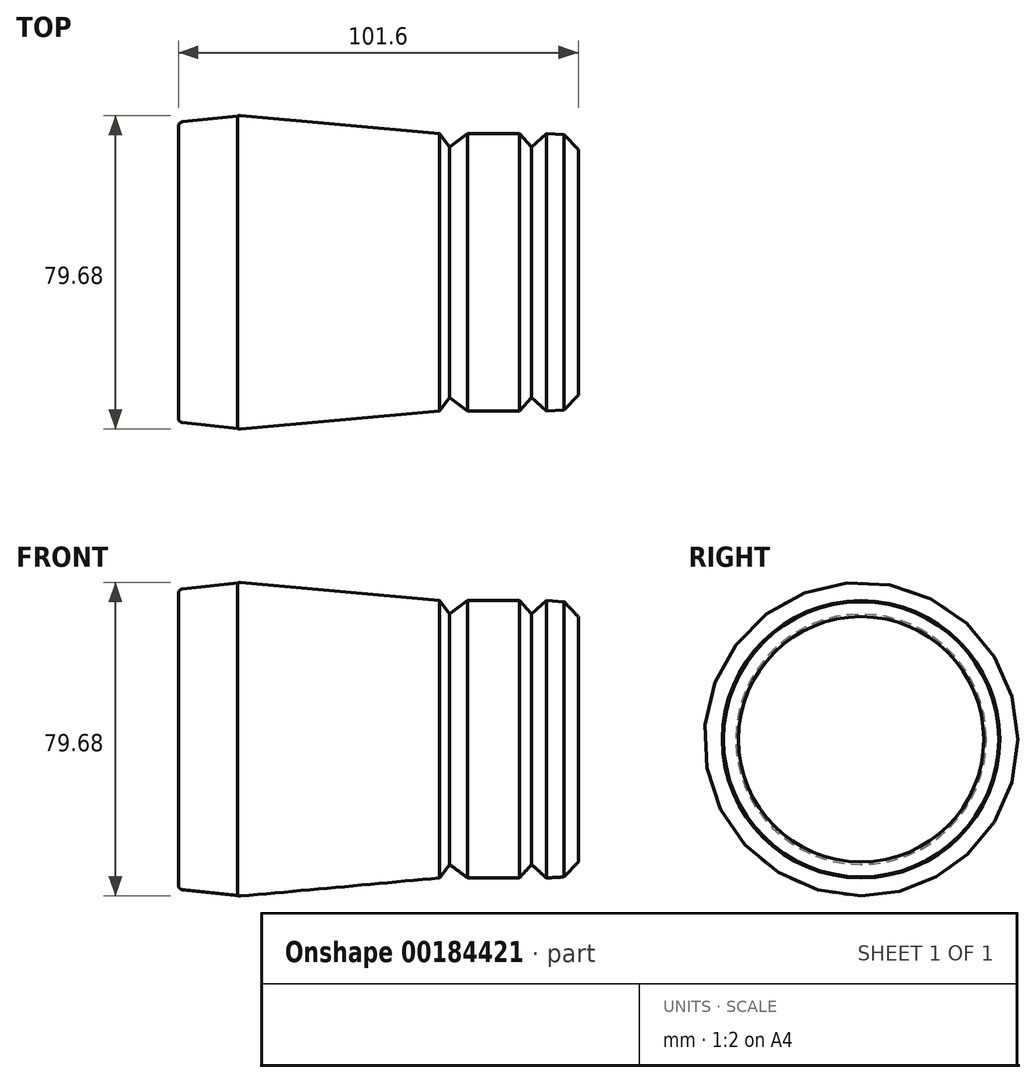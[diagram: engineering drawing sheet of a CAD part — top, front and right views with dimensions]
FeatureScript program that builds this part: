
annotation { "Feature Type Name" : "Feature", "Feature Type Description" : "" }
export const myFeature = defineFeature(function(context is Context, id is Id, definition is map)
    precondition{}
    {
        {
            var Q0;
            Q0=qCreatedBy(makeId("Front.planeOp"),FACE);
            var sketch = newSketch(context, id + "F0", { "sketchPlane" : qUnion([Q0])});
            skLineSegment(sketch, "E0", {"start": v(-60.66, 0) * mm, "end": v(-60.66, 41.28) * mm});
            skLineSegment(sketch, "E1", {"start": v(40.94, 34.75) * mm, "end": v(40.94, 0) * mm});
            skLineSegment(sketch, "E2", {"start": v(40.94, 0) * mm, "end": v(-60.66, 0) * mm});
            skLineSegment(sketch, "E3", {"start": v(-60.66, 41.28) * mm, "end": v(5.7, 35.23) * mm});
            skLineSegment(sketch, "E4", {"start": v(5.7, 35.23) * mm, "end": v(8.27, 31.8) * mm});
            skLineSegment(sketch, "E5", {"start": v(8.27, 31.8) * mm, "end": v(12.84, 35.23) * mm});
            skLineSegment(sketch, "E6", {"start": v(12.84, 35.23) * mm, "end": v(25.96, 35.23) * mm});
            skLineSegment(sketch, "E7", {"start": v(25.96, 35.23) * mm, "end": v(29.1, 31.8) * mm});
            skLineSegment(sketch, "E8", {"start": v(29.1, 31.8) * mm, "end": v(32.83, 35.23) * mm});
            skLineSegment(sketch, "E9", {"start": v(32.83, 35.23) * mm, "end": v(40.94, 34.75) * mm});
            skSolve(sketch);
        }
        {
            var Q0;
            Q0=makeQuery(id+"F0.imprint","IMPRINT",FACE,{"disambiguationData":[TD([[makeQuery(id+"F0.imprint","IMPRINT",EDGE,{"derivedFrom":sQuery(id+"F0.wireOp",EDGE,"E0")}),-1.0]])]});
            var Q1;
            Q1=sQuery(id+"F0.wireOp",EDGE,"E2");
            revolve(context, id + "F1", {"entities" : qUnion([Q0]), "axis" : qUnion([Q1]), "revolveType" : RevolveType.FULL});
        }
        {
            var Q0;
            Q0=makeQuery(id+"F1.opRevolve","SWEPT_FACE",FACE,{"disambiguationData":[OSD([sQuery(id+"F0.wireOp",EDGE,"E0")])]});
            var sketch = newSketch(context, id + "F2", { "sketchPlane" : qUnion([Q0])});
            skCircle(sketch, "E10.0", {"center": v(0, 0) * mm, "radius": 38.1 * mm});
            skSolve(sketch);
        }
        {
            var Q0;
            Q0=makeQuery(id+"F2.imprint","IMPRINT",FACE,{"disambiguationData":[TD([[makeQuery(id+"F2.imprint","IMPRINT",EDGE,{"derivedFrom":sQuery(id+"F2.wireOp",EDGE,"E10.0")}),-1.0]])]});
            extrude(context, id + "F3", {"entities" : qUnion([Q0]), "operationType" : NewBodyOperationType.REMOVE, "oppositeDirection" : true, "depth" : 82.55 * mm, "hasDraft" : true, "draftAngle" : 6 * degree, "draftPullDirection" : true});
        }
        {
            var Q0;
            Q0=makeQuery(id+"F1.opRevolve","SWEPT_EDGE",EDGE,{"disambiguationData":[OSD([sQuery(id+"F0.wireOp",EDGE,"E1"),sQuery(id+"F0.wireOp",EDGE,"E9")])]});
            chamfer(context, id + "F4", {"entities" : qUnion([Q0]), "width" : 3.8 * mm, "tangentPropagation" : true});
        }
        {
            var Q0;
            Q0=makeQuery(id+"F1.opRevolve","SWEPT_EDGE",EDGE,{"disambiguationData":[OSD([sQuery(id+"F0.wireOp",EDGE,"E0"),sQuery(id+"F0.wireOp",EDGE,"E3")])]});
            fillet(context, id + "F5", {"entities" : qUnion([Q0]), "radius" : 1.27 * mm, "tangentPropagation" : true, "allowEdgeOverflow" : false});
        }
        {
            var Q0;
            Q0=makeQuery(id+"F1.opRevolve","SWEPT_FACE",FACE,{"disambiguationData":[OSD([sQuery(id+"F0.wireOp",EDGE,"E0")])]});
            fillet(context, id + "F6", {"entities" : qUnion([Q0]), "radius" : 1.27 * mm, "tangentPropagation" : true, "allowEdgeOverflow" : false});
        }
    });
